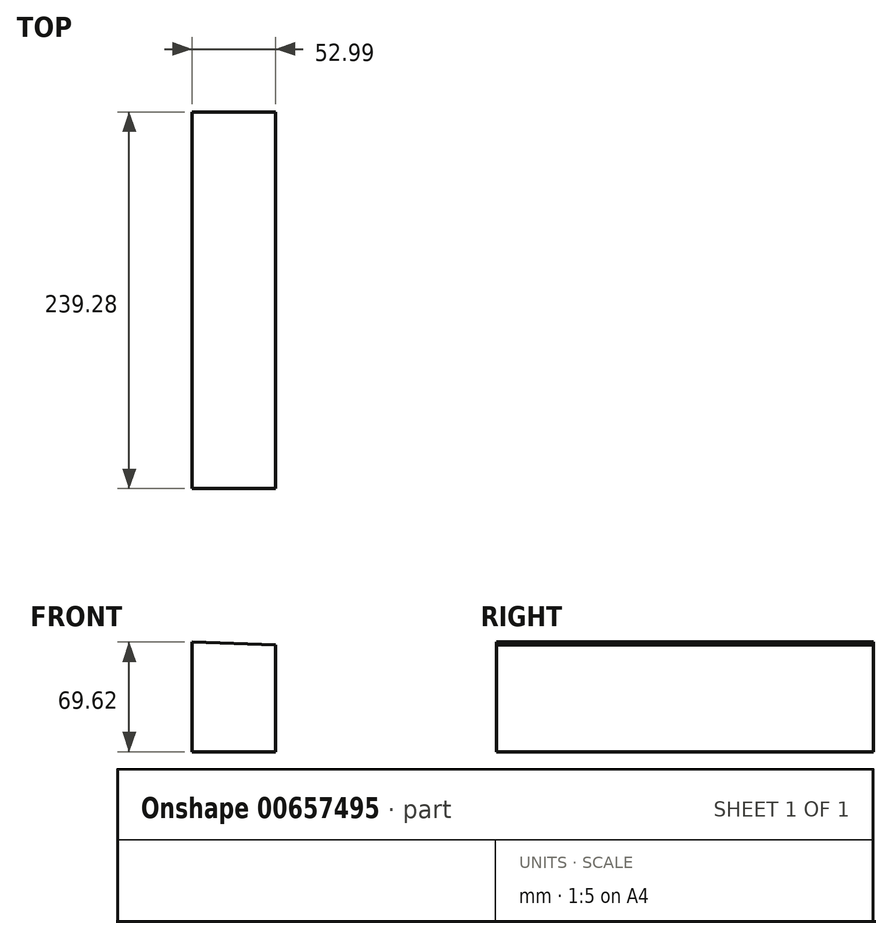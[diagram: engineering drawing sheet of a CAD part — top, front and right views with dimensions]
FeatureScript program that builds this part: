
annotation { "Feature Type Name" : "Feature", "Feature Type Description" : "" }
export const myFeature = defineFeature(function(context is Context, id is Id, definition is map)
    precondition{}
    {
        {
            var Q0;
            Q0=qCreatedBy(makeId("Front.planeOp"),FACE);
            var sketch = newSketch(context, id + "F0", { "sketchPlane" : qUnion([Q0])});
            skLineSegment(sketch, "E0", {"start": v(-34.8, 18.95) * mm, "end": v(-34.8, -50.67) * mm});
            skLineSegment(sketch, "E1", {"start": v(-34.8, -50.67) * mm, "end": v(18.2, -50.67) * mm});
            skLineSegment(sketch, "E2", {"start": v(18.2, -50.67) * mm, "end": v(18.2, 17.24) * mm});
            skLineSegment(sketch, "E3", {"start": v(18.2, 17.24) * mm, "end": v(-34.8, 18.95) * mm});
            skLineSegment(sketch, "E4", {"start": v(65.36, 25.56) * mm, "end": v(65.36, 50) * mm});
            skLineSegment(sketch, "E5", {"start": v(65.36, 50) * mm, "end": v(106.34, 82.97) * mm});
            skSolve(sketch);
        }
        {
            var Q0;
            Q0 = qSketchRegion(id + "F0", true);
            extrude(context, id + "F1", {"entities" : qUnion([Q0]), "depth" : 25.4 * mm, "offsetDistance" : 25.4 * mm});
        }
        {
            var Q0;
            Q0=makeQuery(id+"F1.opExtrude","CAP_FACE",FACE,{"disambiguationData":[OSD([sQuery(id+"F0.wireOp",EDGE,"E0"),sQuery(id+"F0.wireOp",EDGE,"E1"),sQuery(id+"F0.wireOp",EDGE,"E2"),sQuery(id+"F0.wireOp",EDGE,"E3")])],"isStart":false});
            extrude(context, id + "F2", {"entities" : qUnion([Q0]), "operationType" : NewBodyOperationType.ADD, "depth" : 213.88 * mm, "offsetDistance" : 25.4 * mm});
        }
    });
